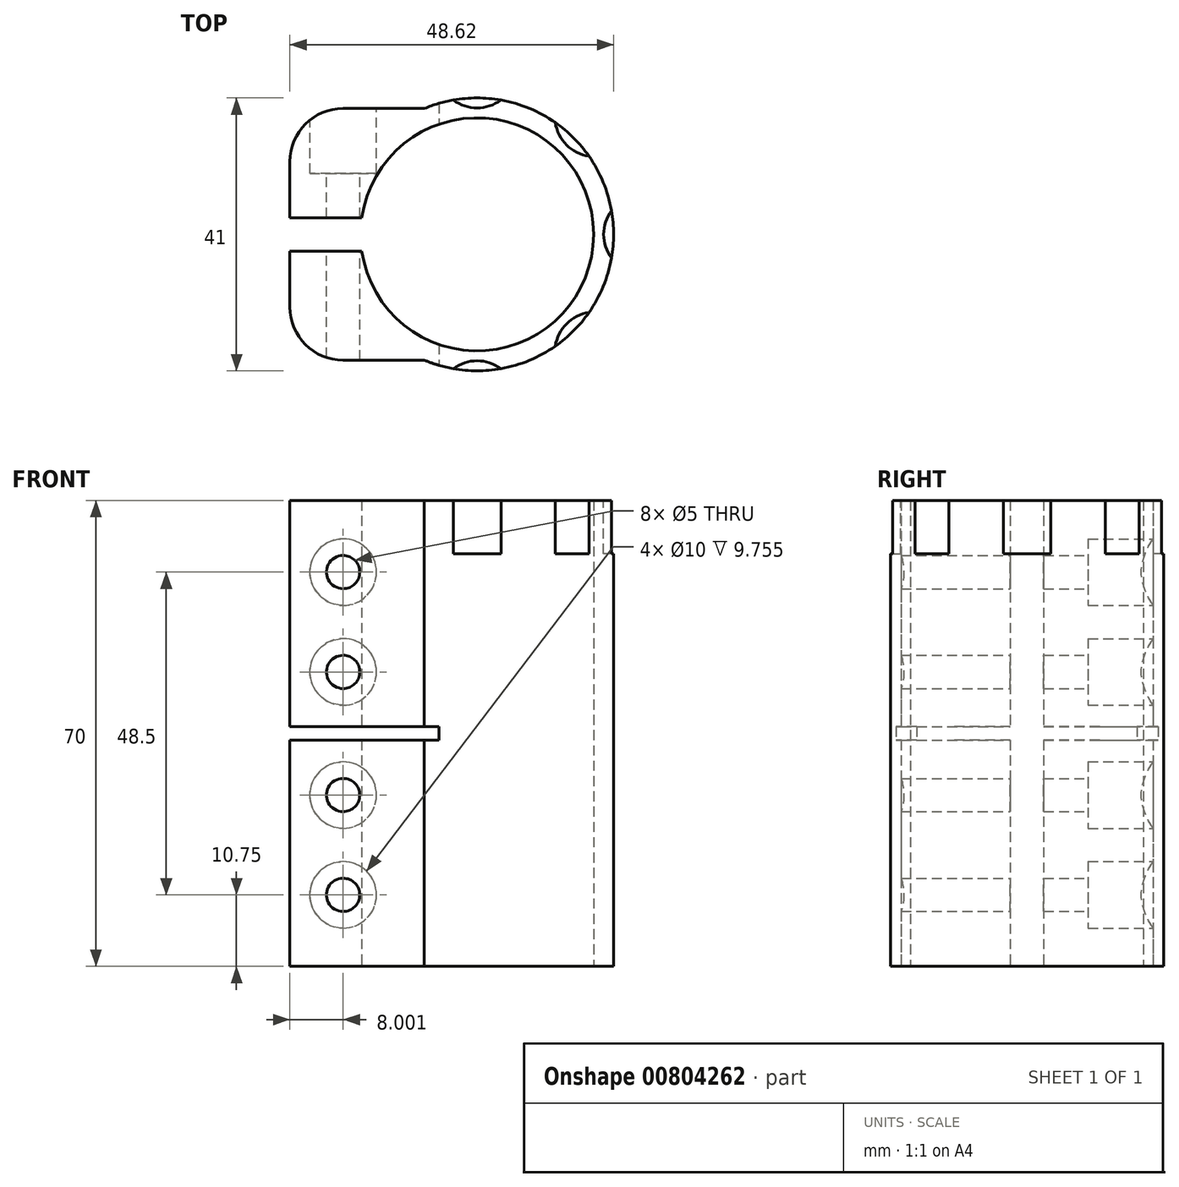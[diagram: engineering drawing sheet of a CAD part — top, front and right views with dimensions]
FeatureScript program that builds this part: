
annotation { "Feature Type Name" : "Feature", "Feature Type Description" : "" }
export const myFeature = defineFeature(function(context is Context, id is Id, definition is map)
    precondition{}
    {
        {
            var Q0;
            Q0=qCreatedBy(makeId("Top.planeOp"),FACE);
            var sketch = newSketch(context, id + "F0", { "sketchPlane" : qUnion([Q0])});
            skArc(sketch, "E0", {"start": v(-17.32, -2.5) * mm, "mid": v(17.5, 0) * mm, "end": v(-17.32, 2.5) * mm});
            skLineSegment(sketch, "E1", {"start": v(-17.32, 2.5) * mm, "end": v(-28.12, 2.5) * mm});
            skLineSegment(sketch, "E2", {"start": v(-28.12, 2.5) * mm, "end": v(-28.12, 10.9) * mm});
            skLineSegment(sketch, "E3", {"start": v(-20.12, 18.9) * mm, "end": v(-7.92, 18.9) * mm});
            skPoint(sketch, "E4.visualSharp", {"position": v(-28.12, 18.9) * mm});
            skArc(sketch, "E4.filletArc", {"start": v(-20.12, 18.9) * mm, "mid": v(-25.78, 16.57) * mm, "end": v(-28.12, 10.9) * mm});
            skLineSegment(sketch, "E5", {"start": v(0, 0) * mm, "end": v(40.24, 0) * mm, "construction": true});
            skLineSegment(sketch, "E6.MirrorCS", {"start": v(-20.12, -18.9) * mm, "end": v(-7.92, -18.9) * mm});
            skArc(sketch, "E7.MirrorCS", {"start": v(-20.12, -18.9) * mm, "mid": v(-25.78, -16.57) * mm, "end": v(-28.12, -10.9) * mm});
            skLineSegment(sketch, "E8.MirrorCS", {"start": v(-28.12, -2.5) * mm, "end": v(-28.12, -10.9) * mm});
            skLineSegment(sketch, "E9.MirrorCS", {"start": v(-17.32, -2.5) * mm, "end": v(-28.12, -2.5) * mm});
            skArc(sketch, "E10.trimOffspring", {"start": v(-7.92, -18.9) * mm, "mid": v(20.5, 0) * mm, "end": v(-7.92, 18.9) * mm});
            skSolve(sketch);
        }
        {
            var Q0;
            Q0 = qSketchRegion(id + "F0", true);
            extrude(context, id + "F1", {"entities" : qUnion([Q0]), "endBound" : BoundingType.SYMMETRIC, "depth" : 70 * mm, "offsetDistance" : 25 * mm});
        }
        {
            var Q0;
            Q0=makeQuery(id+"F1.opExtrude","SWEPT_FACE",FACE,{"disambiguationData":[OSD([sQuery(id+"F0.wireOp",EDGE,"E3")])]});
            var sketch = newSketch(context, id + "F2", { "sketchPlane" : qUnion([Q0])});
            skPoint(sketch, "E11", {"position": v(20.12, -24.25) * mm});
            skPoint(sketch, "E12", {"position": v(20.12, -9.25) * mm});
            skPoint(sketch, "E13", {"position": v(20.12, 9.25) * mm});
            skPoint(sketch, "E14", {"position": v(20.12, 24.25) * mm});
            skSolve(sketch);
        }
        {
            var Q0;
            Q0=sQuery(id+"F2.wireOp",VERTEX,"E11");
            var Q1;
            Q1=sQuery(id+"F2.wireOp",VERTEX,"E12");
            var Q2;
            Q2=sQuery(id+"F2.wireOp",VERTEX,"E13");
            var Q3;
            Q3=sQuery(id+"F2.wireOp",VERTEX,"E14");
            var Q4;
            Q4=makeQuery(id+"F1.opExtrude","SWEPT_BODY",BODY,{"disambiguationData":[OSD([sQuery(id+"F0.wireOp",EDGE,"E0"),sQuery(id+"F0.wireOp",EDGE,"E1"),sQuery(id+"F0.wireOp",EDGE,"E2"),sQuery(id+"F0.wireOp",EDGE,"E3"),sQuery(id+"F0.wireOp",EDGE,"E4.filletArc"),sQuery(id+"F0.wireOp",EDGE,"E6.MirrorCS"),sQuery(id+"F0.wireOp",EDGE,"E7.MirrorCS"),sQuery(id+"F0.wireOp",EDGE,"E8.MirrorCS"),sQuery(id+"F0.wireOp",EDGE,"E9.MirrorCS"),sQuery(id+"F0.wireOp",EDGE,"E10.trimOffspring")])]});
            hole(context, id + "F3", {"style" : HoleStyle.C_BORE, "endStyle" : HoleEndStyle.THROUGH, "holeDiameter" : 5 * mm, "cBoreDiameter" : 10 * mm, "cBoreDepth" : 8 * mm, "majorDiameter" : 5 * mm, "isTappedThrough" : true, "tappedDepth" : 12 * mm, "tapClearance" : 3, "locations" : qUnion([Q0, Q1, Q2, Q3]), "scope" : qUnion([Q4])});
        }
        {
            var Q0;
            Q0=qCreatedBy(makeId("Front.planeOp"),FACE);
            var sketch = newSketch(context, id + "F4", { "sketchPlane" : qUnion([Q0])});
            skLineSegment(sketch, "E15.bottom", {"start": v(-28.12, -1) * mm, "end": v(-5.72, -1) * mm});
            skLineSegment(sketch, "E15.top", {"start": v(-28.12, 1) * mm, "end": v(-5.72, 1) * mm});
            skLineSegment(sketch, "E15.left", {"start": v(-28.12, -1) * mm, "end": v(-28.12, 1) * mm});
            skLineSegment(sketch, "E15.right", {"start": v(-5.72, -1) * mm, "end": v(-5.72, 1) * mm});
            skSolve(sketch);
        }
        {
            var Q0;
            Q0 = qSketchRegion(id + "F4", true);
            extrude(context, id + "F5", {"entities" : qUnion([Q0]), "operationType" : NewBodyOperationType.REMOVE, "endBound" : BoundingType.SYMMETRIC, "oppositeDirection" : true, "depth" : 50 * mm, "offsetDistance" : 25 * mm});
        }
        {
            var Q0;
            Q0=makeQuery(id+"F1.opExtrude","CAP_FACE",FACE,{"disambiguationData":[OSD([sQuery(id+"F0.wireOp",EDGE,"E0"),sQuery(id+"F0.wireOp",EDGE,"E1"),sQuery(id+"F0.wireOp",EDGE,"E2"),sQuery(id+"F0.wireOp",EDGE,"E3"),sQuery(id+"F0.wireOp",EDGE,"E4.filletArc"),sQuery(id+"F0.wireOp",EDGE,"E6.MirrorCS"),sQuery(id+"F0.wireOp",EDGE,"E7.MirrorCS"),sQuery(id+"F0.wireOp",EDGE,"E8.MirrorCS"),sQuery(id+"F0.wireOp",EDGE,"E9.MirrorCS"),sQuery(id+"F0.wireOp",EDGE,"E10.trimOffspring")])],"isStart":false});
            var sketch = newSketch(context, id + "F6", { "sketchPlane" : qUnion([Q0])});
            skPoint(sketch, "E16.center", {"position": v(0, 0) * mm});
            skCircle(sketch, "E17", {"center": v(0, -25) * mm, "radius": 6 * mm});
            skCircle(sketch, "E18.1.0", {"center": v(17.68, -17.68) * mm, "radius": 6 * mm});
            skCircle(sketch, "E18.2.0", {"center": v(25, 0) * mm, "radius": 6 * mm});
            skCircle(sketch, "E18.3.0", {"center": v(17.68, 17.68) * mm, "radius": 6 * mm});
            skCircle(sketch, "E18.4.0", {"center": v(0, 25) * mm, "radius": 6 * mm});
            skLineSegment(sketch, "E18.anchor1", {"start": v(0, 0) * mm, "end": v(0, -25) * mm, "construction": true});
            skLineSegment(sketch, "E18.anchor2", {"start": v(0, 0) * mm, "end": v(0, 25) * mm, "construction": true});
            skSolve(sketch);
        }
        {
            var Q0;
            Q0=makeQuery(id+"F6.imprint","IMPRINT",FACE,{"disambiguationData":[TD([[makeQuery(id+"F6.imprint","IMPRINT",EDGE,{"derivedFrom":sQuery(id+"F6.wireOp",EDGE,"E18.4.0")}),1.0]])]});
            var Q1;
            Q1=makeQuery(id+"F6.imprint","IMPRINT",FACE,{"disambiguationData":[TD([[makeQuery(id+"F6.imprint","IMPRINT",EDGE,{"derivedFrom":sQuery(id+"F6.wireOp",EDGE,"E18.3.0")}),1.0]])]});
            var Q2;
            Q2=makeQuery(id+"F6.imprint","IMPRINT",FACE,{"disambiguationData":[TD([[makeQuery(id+"F6.imprint","IMPRINT",EDGE,{"derivedFrom":sQuery(id+"F6.wireOp",EDGE,"E18.2.0")}),1.0]])]});
            var Q3;
            Q3=makeQuery(id+"F6.imprint","IMPRINT",FACE,{"disambiguationData":[TD([[makeQuery(id+"F6.imprint","IMPRINT",EDGE,{"derivedFrom":sQuery(id+"F6.wireOp",EDGE,"E18.1.0")}),1.0]])]});
            var Q4;
            Q4=makeQuery(id+"F6.imprint","IMPRINT",FACE,{"disambiguationData":[TD([[makeQuery(id+"F6.imprint","IMPRINT",EDGE,{"derivedFrom":sQuery(id+"F6.wireOp",EDGE,"E17")}),1.0]])]});
            extrude(context, id + "F7", {"entities" : qUnion([Q0, Q1, Q2, Q3, Q4]), "operationType" : NewBodyOperationType.REMOVE, "oppositeDirection" : true, "depth" : 8 * mm, "offsetDistance" : 25 * mm});
        }
    });
